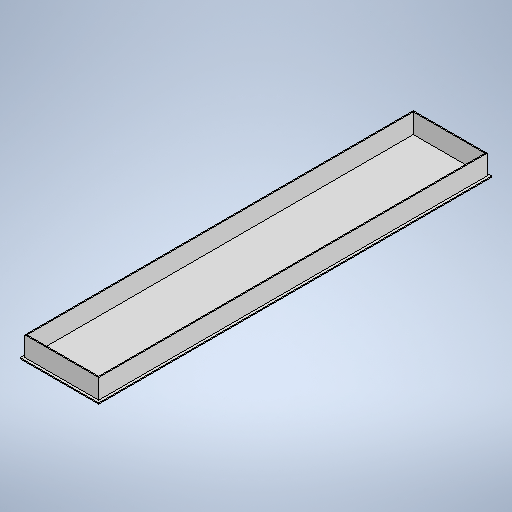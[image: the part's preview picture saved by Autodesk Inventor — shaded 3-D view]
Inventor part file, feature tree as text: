
AUTODESK INVENTOR PART (.ipt)
format: ipt  version: 2025 (Build 290162010, 162A)  size: 246,784 bytes
history: native  units: mm
features: extrude x2, sketch x2, projected_geometry x1
ambient origin geometry x8: Origin, YZ Plane, XZ Plane, XY Plane, X Axis, Y Axis, Z Axis, Center Point
bodies: Solid1 (feature_tree)
feature tree (5):
  extrude  "Extrusion1"  Depth=4000.0mm
  extrude  "Extrusion2"  Depth=25.0mm
  sketch  "Sketch1"  dims[d0=800.0mm d1=4000.0mm]
  sketch  "Sketch2"  dims[d2=10.0mm d3=0.0mm d4=25.0mm d5=10.0mm d6=200.0mm d7=0.0mm]
  projected_geometry  "Projected Loop1"
